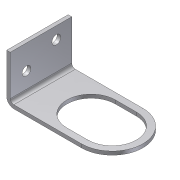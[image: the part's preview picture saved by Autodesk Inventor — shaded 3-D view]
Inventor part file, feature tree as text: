
AUTODESK INVENTOR PART (.ipt)
format: ipt  version: 2013 (Build 170138000, 138)  size: 120,320 bytes
history: native  units: mm (DEFAULTED — no unit token found)
features: sheet_metal_op x3, sketch x3, other x3, projected_geometry x1
ambient origin geometry x8: Origin, YZ Plane, XZ Plane, XY Plane, X Axis, Y Axis, Z Axis, Center Point
bodies: Solid1 (feature_tree)
feature tree (10):
  sheet_metal_op  "Face1"
  sheet_metal_op  "Flange1"
  sketch  "Sketch1"  dims[d0=38.0mm]
  other  "Plate1"
  sketch  "Sketch2"  dims[d1=63.0mm]
  other  "Plate2"
  sheet_metal_op  "Bend1"
  sketch  "Sketch3"  dims[d2=4.0mm d3=43.0mm d4=2.2mm d5=2.2mm d6=1.1mm d7=4.4mm d8=2.2mm d9=27.0mm d10=90.0deg d11=2.2mm d12=5.5mm d13=9.5mm d14=7.5mm d15=10.0mm d16=15.0mm d17=2.2mm d18=0.0mm]
  projected_geometry  "Projected Loop1"
  other  "Cut1"
